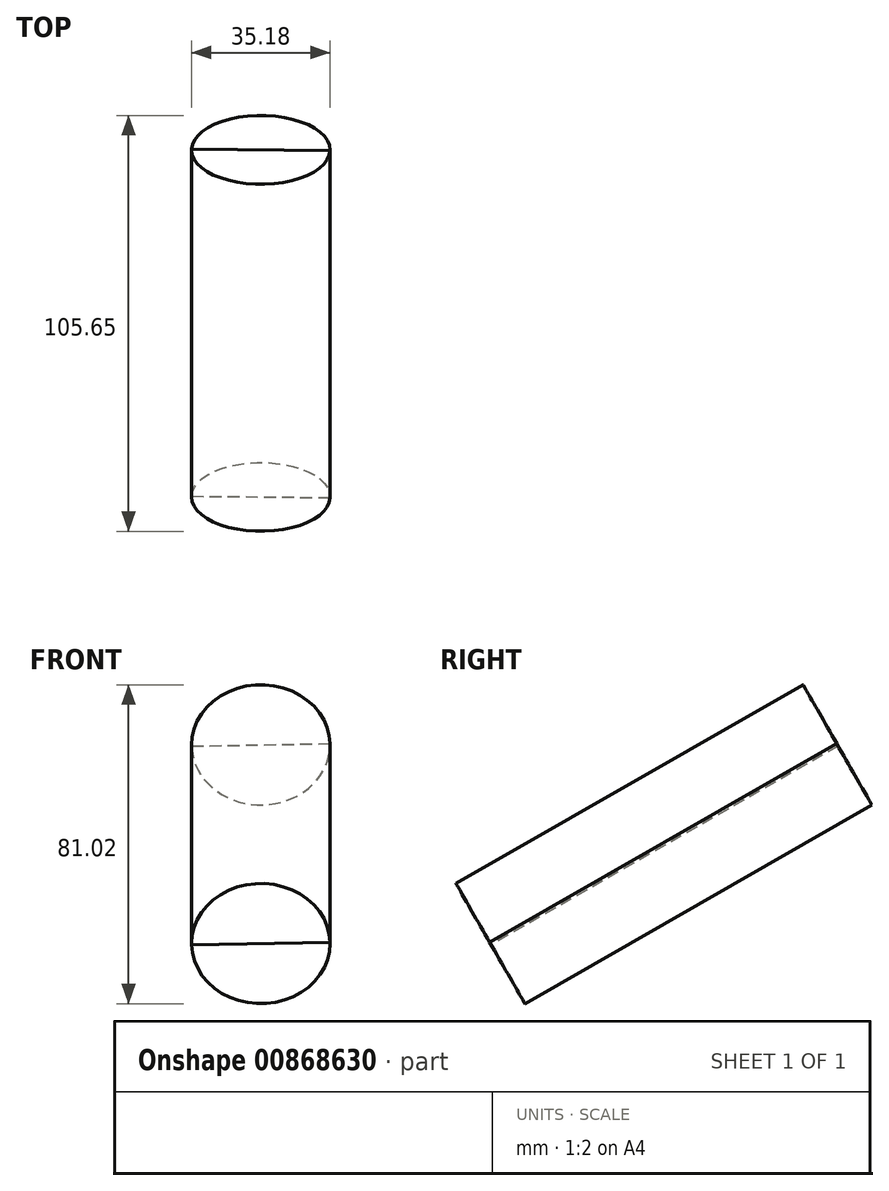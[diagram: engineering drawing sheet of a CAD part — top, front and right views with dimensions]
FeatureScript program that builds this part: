
annotation { "Feature Type Name" : "Feature", "Feature Type Description" : "" }
export const myFeature = defineFeature(function(context is Context, id is Id, definition is map)
    precondition{}
    {
        {
            var Q0;
            Q0=qCreatedBy(makeId("Right.planeOp"),FACE);
            var sketch = newSketch(context, id + "F0", { "sketchPlane" : qUnion([Q0])});
            skCircle(sketch, "E0", {"center": v(557.98, 431.54) * mm, "radius": 330.2 * mm});
            skLineSegment(sketch, "E1", {"start": v(1167.19, 883.1) * mm, "end": v(1252.5, 931.94) * mm});
            skSolve(sketch);
        }
        {
            var Q0;
            Q0=sQuery(id+"F0.wireOp",VERTEX,"E1.start");
            var Q1;
            Q1=sQuery(id+"F0.wireOp",EDGE,"E1");
            cPlane(context, id + "F1", {"entities" : qUnion([Q0, Q1]), "cplaneType" : CPlaneType.LINE_POINT, "offset" : 25.4 * mm, "width" : 152.4 * mm, "height" : 152.4 * mm});
        }
        {
            var Q0;
            Q0=qCreatedBy(id+"F1.planeOp",FACE);
            var sketch = newSketch(context, id + "F2", { "sketchPlane" : qUnion([Q0])});
            skArc(sketch, "E2", {"start": v(17.59, 186.02) * mm, "mid": v(0.38, 203.98) * mm, "end": v(-17.59, 186.77) * mm});
            skLineSegment(sketch, "E3", {"start": v(17.59, 186.02) * mm, "end": v(-17.59, 186.77) * mm});
            skSolve(sketch);
        }
        {
            var Q0;
            Q0=makeQuery(id+"F2.imprint","IMPRINT",FACE,{"disambiguationData":[TD([[makeQuery(id+"F2.imprint","IMPRINT",EDGE,{"derivedFrom":sQuery(id+"F2.wireOp",EDGE,"E2")}),1.0]])]});
            extrude(context, id + "F3", {"entities" : qUnion([Q0]), "depth" : 101.6 * mm, "offsetDistance" : 25.4 * mm});
        }
        {
            var Q0;
            Q0=makeQuery(id+"F3.opExtrude","SWEPT_FACE",FACE,{"disambiguationData":[OSD([sQuery(id+"F2.wireOp",EDGE,"E3")])]});
            cPlane(context, id + "F4", {"entities" : qUnion([Q0]), "cplaneType" : CPlaneType.OFFSET, "offset" : 0 * mm, "width" : 152.4 * mm, "height" : 152.4 * mm});
        }
        {
            var Q0;
            Q0=makeQuery(id+"F3.opExtrude","SWEPT_BODY",BODY,{"disambiguationData":[OSD([sQuery(id+"F2.wireOp",EDGE,"E2"),sQuery(id+"F2.wireOp",EDGE,"E3")])]});
            var Q1;
            Q1=qCreatedBy(id+"F4.planeOp",FACE);
            mirror(context, id + "F5", {"entities" : qUnion([Q0]), "mirrorPlane" : qUnion([Q1])});
        }
    });
